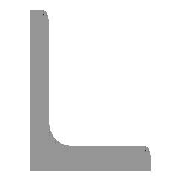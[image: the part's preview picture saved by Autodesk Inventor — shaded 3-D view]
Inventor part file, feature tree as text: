
AUTODESK INVENTOR PART (.ipt)
format: ipt  version: 2022 (Build 260153000, 153)  size: 171,008 bytes
history: native  units: mm (DEFAULTED — no unit token found)
features: other x5, sketch x2, sweep x1, plane x1
ambient origin geometry x8: Origin, YZ Plane, XZ Plane, XY Plane, X Axis, Y Axis, Z Axis, Center Point
bodies: Solid1 (feature_tree), Body (feature_tree)
feature tree (9):
  parser-record x1  (decoder bookkeeping rows leaked as tree rows — omitted from the tree; the rows remain in map.json)
  other  "Driven Length"
  other  "Start plane"
  other  "End plane"
  sweep  "Sweep Path"
  other  "Orientation Work Plane"
  sketch  "Sketch3"  dims[d3=50.0mm d4=60.0mm]
  plane  "Work Plane10"
  sketch  "Sketch4"  dims[d5=50.0mm d6=60.0mm d7=4.0mm d8=8.0mm d9=4.0mm d10=8.0mm d17=8.0mm d18=4.0mm d19=17.7mm d20=17.7mm d21=-0.0mm d22=2815.406592mm d23=90.0deg d24=2815.406592mm d25=0.0mm d26=0.0mm]
